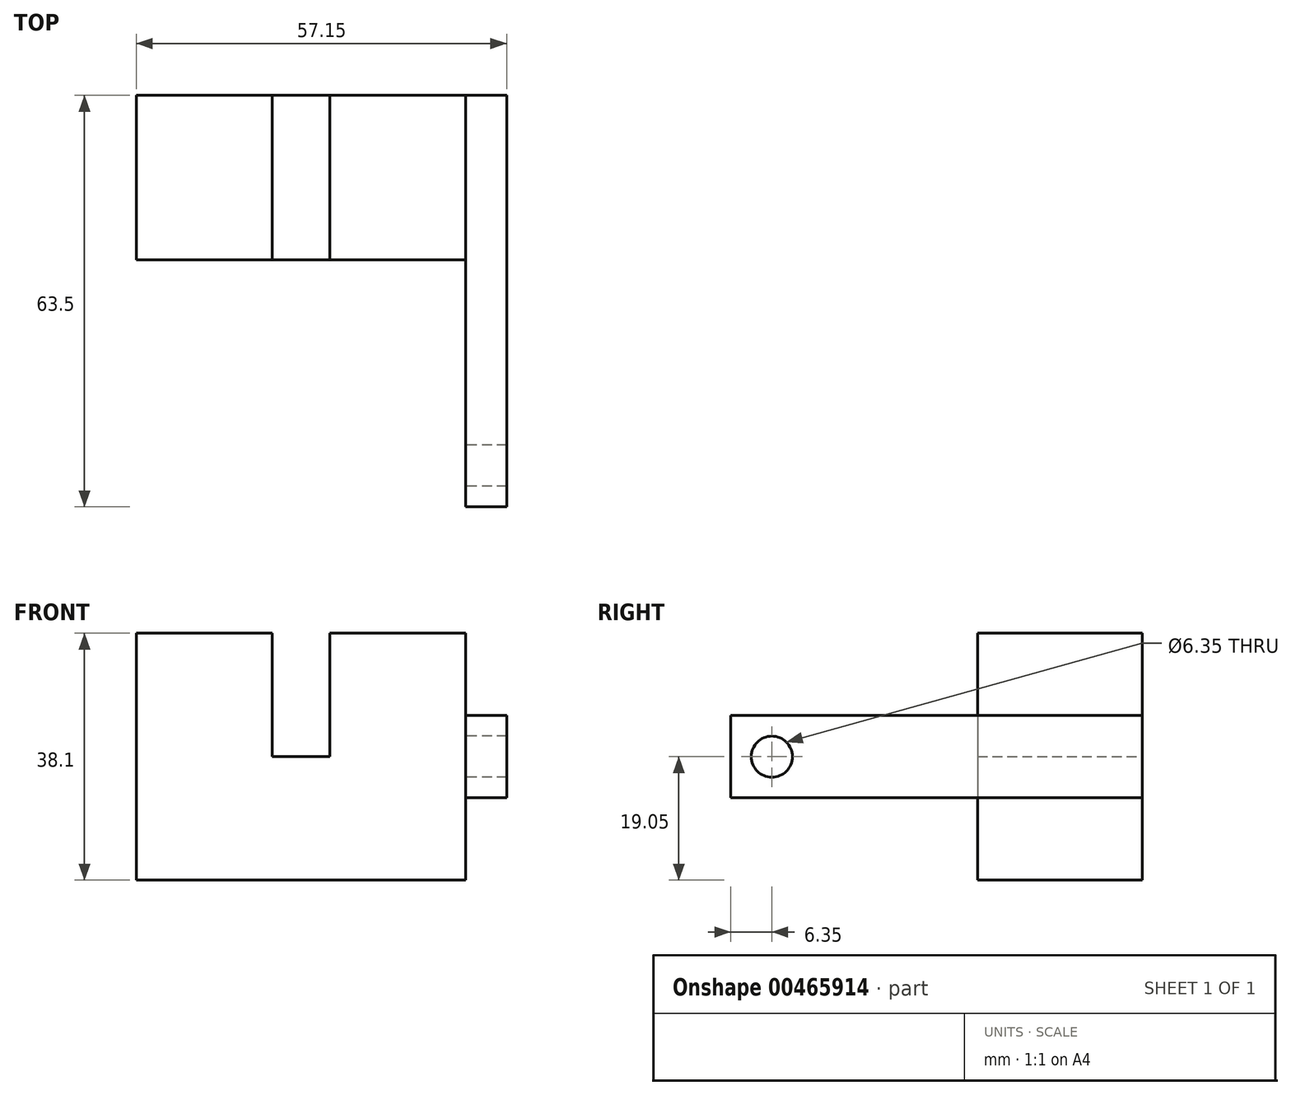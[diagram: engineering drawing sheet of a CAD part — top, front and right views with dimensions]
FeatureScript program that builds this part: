
annotation { "Feature Type Name" : "Feature", "Feature Type Description" : "" }
export const myFeature = defineFeature(function(context is Context, id is Id, definition is map)
    precondition{}
    {
        {
            var Q0;
            Q0=qCreatedBy(makeId("Front.planeOp"),FACE);
            var sketch = newSketch(context, id + "F0", { "sketchPlane" : qUnion([Q0])});
            skLineSegment(sketch, "E0.bottom", {"start": v(-25.4, 19.05) * mm, "end": v(25.4, 19.05) * mm});
            skLineSegment(sketch, "E0.top", {"start": v(-25.4, -19.05) * mm, "end": v(25.4, -19.05) * mm});
            skLineSegment(sketch, "E0.left", {"start": v(-25.4, 19.05) * mm, "end": v(-25.4, -19.05) * mm});
            skLineSegment(sketch, "E0.right", {"start": v(25.4, 19.05) * mm, "end": v(25.4, -19.05) * mm});
            skPoint(sketch, "E0.middle", {"position": v(0, 0) * mm});
            skLineSegment(sketch, "E1", {"start": v(0, 0) * mm, "end": v(0, 19.05) * mm});
            skLineSegment(sketch, "E2", {"start": v(0, 19.05) * mm, "end": v(-4.45, 19.05) * mm});
            skLineSegment(sketch, "E3", {"start": v(0, 19.05) * mm, "end": v(4.44, 19.05) * mm});
            skLineSegment(sketch, "E4", {"start": v(4.44, 19.05) * mm, "end": v(4.44, 0) * mm});
            skLineSegment(sketch, "E5", {"start": v(-4.45, 19.05) * mm, "end": v(-4.45, 0) * mm});
            skLineSegment(sketch, "E6", {"start": v(-4.45, 0) * mm, "end": v(4.44, 0) * mm});
            skSolve(sketch);
        }
        {
            var Q0;
            Q0=makeQuery(id+"F0.imprint","IMPRINT",FACE,{"disambiguationData":[TD([[makeQuery(id+"F0.imprint","IMPRINT",EDGE,{"derivedFrom":sQuery(id+"F0.wireOp",EDGE,"E0.top")}),1.0]])]});
            extrude(context, id + "F1", {"entities" : qUnion([Q0]), "depth" : 25.4 * mm});
        }
        {
            var Q0;
            Q0=qCreatedBy(makeId("Front.planeOp"),FACE);
            var sketch = newSketch(context, id + "F2", { "sketchPlane" : qUnion([Q0])});
            skLineSegment(sketch, "E7", {"start": v(0, 0) * mm, "end": v(25.4, 0) * mm});
            skLineSegment(sketch, "E8", {"start": v(25.4, 0) * mm, "end": v(31.75, 0) * mm});
            skLineSegment(sketch, "E9", {"start": v(31.75, 0) * mm, "end": v(31.75, 6.35) * mm});
            skLineSegment(sketch, "E10", {"start": v(31.75, 6.35) * mm, "end": v(31.75, -6.35) * mm});
            skPoint(sketch, "E10.endSnap0", {"position": v(31.75, 3.18) * mm});
            skLineSegment(sketch, "E11", {"start": v(31.75, -6.35) * mm, "end": v(25.4, -6.35) * mm});
            skLineSegment(sketch, "E12", {"start": v(25.4, -6.35) * mm, "end": v(25.4, 6.35) * mm});
            skLineSegment(sketch, "E13", {"start": v(25.4, 6.35) * mm, "end": v(31.75, 6.35) * mm});
            skSolve(sketch);
        }
        {
            var Q0;
            {var subQ0=sQuery(id+"F2.wireOp",EDGE,"E8");Q0=makeQuery(id+"F2.imprint","IMPRINT",FACE,{"disambiguationData":[TD([[makeQuery(id+"F2.imprint","IMPRINT",EDGE,{"derivedFrom":subQ0}),-1.0]])]});}
            var Q1;
            {var subQ0=sQuery(id+"F2.wireOp",EDGE,"E8");Q1=makeQuery(id+"F2.imprint","IMPRINT",FACE,{"disambiguationData":[TD([[makeQuery(id+"F2.imprint","IMPRINT",EDGE,{"derivedFrom":subQ0}),1.0]])]});}
            extrude(context, id + "F3", {"entities" : qUnion([Q0, Q1]), "operationType" : NewBodyOperationType.ADD, "depth" : 63.5 * mm});
        }
        {
            var Q0;
            Q0=qCreatedBy(makeId("Right.planeOp"),FACE);
            var sketch = newSketch(context, id + "F4", { "sketchPlane" : qUnion([Q0])});
            skLineSegment(sketch, "E14", {"start": v(0, 0) * mm, "end": v(-57.15, 0) * mm});
            skCircle(sketch, "E15", {"center": v(-57.15, 0) * mm, "radius": 3.18 * mm});
            skSolve(sketch);
        }
        {
            var Q0;
            Q0 = qSketchRegion(id + "F4", true);
            extrude(context, id + "F5", {"entities" : qUnion([Q0]), "operationType" : NewBodyOperationType.REMOVE, "endBound" : BoundingType.SYMMETRIC, "depth" : 127 * mm});
        }
    });
